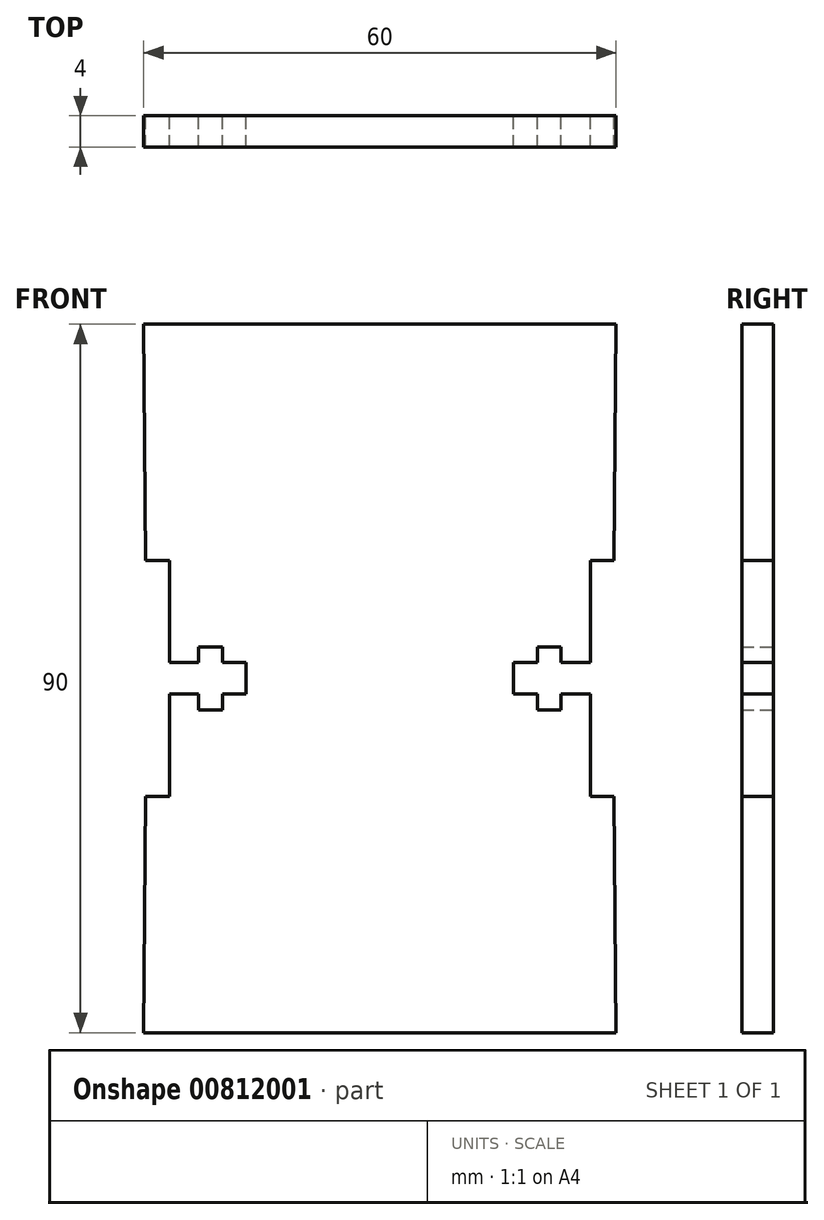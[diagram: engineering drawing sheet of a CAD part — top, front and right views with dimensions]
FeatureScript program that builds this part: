
annotation { "Feature Type Name" : "Feature", "Feature Type Description" : "" }
export const myFeature = defineFeature(function(context is Context, id is Id, definition is map)
    precondition{}
    {
        {
            var Q0;
            Q0=qCreatedBy(makeId("Front.planeOp"),FACE);
            var sketch = newSketch(context, id + "F0", { "sketchPlane" : qUnion([Q0])});
            skLineSegment(sketch, "E0", {"start": v(30, 45) * mm, "end": v(-30, 45) * mm});
            skLineSegment(sketch, "E1", {"start": v(-30, -45) * mm, "end": v(30, -45) * mm});
            skLineSegment(sketch, "E2.0", {"start": v(17, 0) * mm, "end": v(17, 2) * mm});
            skLineSegment(sketch, "E3", {"start": v(29.73, 15) * mm, "end": v(26.73, 15) * mm});
            skLineSegment(sketch, "E4", {"start": v(26.73, 15) * mm, "end": v(26.73, 2) * mm});
            skLineSegment(sketch, "E5", {"start": v(26.73, -15) * mm, "end": v(29.73, -15) * mm});
            skLineSegment(sketch, "E6.0", {"start": v(17, 2) * mm, "end": v(20, 2) * mm});
            skLineSegment(sketch, "E7.0", {"start": v(20, 2) * mm, "end": v(20, 4) * mm});
            skLineSegment(sketch, "E8.0", {"start": v(23, 2) * mm, "end": v(23, 4) * mm});
            skLineSegment(sketch, "E9.trimOffspring", {"start": v(23, 2) * mm, "end": v(26.73, 2) * mm});
            skLineSegment(sketch, "E10.trimOffspring", {"start": v(26.73, 15) * mm, "end": v(29.73, 15) * mm});
            skLineSegment(sketch, "E11.trimOffspring", {"start": v(20, 4) * mm, "end": v(23, 4) * mm});
            skLineSegment(sketch, "E12.MirrorCS", {"start": v(17, 0) * mm, "end": v(17, -2) * mm});
            skLineSegment(sketch, "E13.MirrorCS", {"start": v(17, -2) * mm, "end": v(20, -2) * mm});
            skLineSegment(sketch, "E14.MirrorCS", {"start": v(20, -4) * mm, "end": v(23, -4) * mm});
            skLineSegment(sketch, "E15.MirrorCS", {"start": v(23, -2) * mm, "end": v(26.73, -2) * mm});
            skLineSegment(sketch, "E16.MirrorCS", {"start": v(26.73, -15) * mm, "end": v(26.73, -2) * mm});
            skLineSegment(sketch, "E17.MirrorCS", {"start": v(29.73, -15) * mm, "end": v(26.73, -15) * mm});
            skLineSegment(sketch, "E18.MirrorCS", {"start": v(20, -2) * mm, "end": v(20, -4) * mm});
            skLineSegment(sketch, "E19.MirrorCS", {"start": v(23, -2) * mm, "end": v(23, -4) * mm});
            skLineSegment(sketch, "E20", {"start": v(0, 45) * mm, "end": v(0, -45) * mm});
            skLineSegment(sketch, "E21.MirrorCS", {"start": v(-29.73, 15) * mm, "end": v(-26.73, 15) * mm});
            skLineSegment(sketch, "E22.MirrorCS", {"start": v(-26.73, 15) * mm, "end": v(-26.73, 2) * mm});
            skLineSegment(sketch, "E23.MirrorCS", {"start": v(-23, 2) * mm, "end": v(-26.73, 2) * mm});
            skLineSegment(sketch, "E24.MirrorCS", {"start": v(-23, 2) * mm, "end": v(-23, 4) * mm});
            skLineSegment(sketch, "E25.MirrorCS", {"start": v(-20, 4) * mm, "end": v(-23, 4) * mm});
            skLineSegment(sketch, "E26.MirrorCS", {"start": v(-20, 2) * mm, "end": v(-20, 4) * mm});
            skLineSegment(sketch, "E27.MirrorCS", {"start": v(-17, 2) * mm, "end": v(-20, 2) * mm});
            skLineSegment(sketch, "E28.MirrorCS", {"start": v(-17, 0) * mm, "end": v(-17, 2) * mm});
            skLineSegment(sketch, "E29.MirrorCS", {"start": v(-17, -2) * mm, "end": v(-20, -2) * mm});
            skLineSegment(sketch, "E30.MirrorCS", {"start": v(-17, 0) * mm, "end": v(-17, -2) * mm});
            skLineSegment(sketch, "E31.MirrorCS", {"start": v(-20, -2) * mm, "end": v(-20, -4) * mm});
            skLineSegment(sketch, "E32.MirrorCS", {"start": v(-20, -4) * mm, "end": v(-23, -4) * mm});
            skLineSegment(sketch, "E33.MirrorCS", {"start": v(-23, -2) * mm, "end": v(-23, -4) * mm});
            skLineSegment(sketch, "E34.MirrorCS", {"start": v(-23, -2) * mm, "end": v(-26.73, -2) * mm});
            skLineSegment(sketch, "E35.MirrorCS", {"start": v(-26.73, -15) * mm, "end": v(-26.73, -2) * mm});
            skLineSegment(sketch, "E36.MirrorCS", {"start": v(-29.73, -15) * mm, "end": v(-26.73, -15) * mm});
            skLineSegment(sketch, "E37", {"start": v(-30, 45) * mm, "end": v(-29.73, 15) * mm});
            skLineSegment(sketch, "E38", {"start": v(-29.73, -15) * mm, "end": v(-30, -45) * mm});
            skPoint(sketch, "E39.end.orphan", {"position": v(30, 0) * mm});
            skLineSegment(sketch, "E40", {"start": v(30, 45) * mm, "end": v(29.73, 15) * mm});
            skLineSegment(sketch, "E41", {"start": v(29.73, -15) * mm, "end": v(30, -45) * mm});
            skSolve(sketch);
        }
        {
            var Q0;
            Q0 = qSketchRegion(id + "F0", true);
            extrude(context, id + "F1", {"entities" : qUnion([Q0]), "depth" : 4 * mm, "offsetDistance" : 25 * mm});
        }
    });
